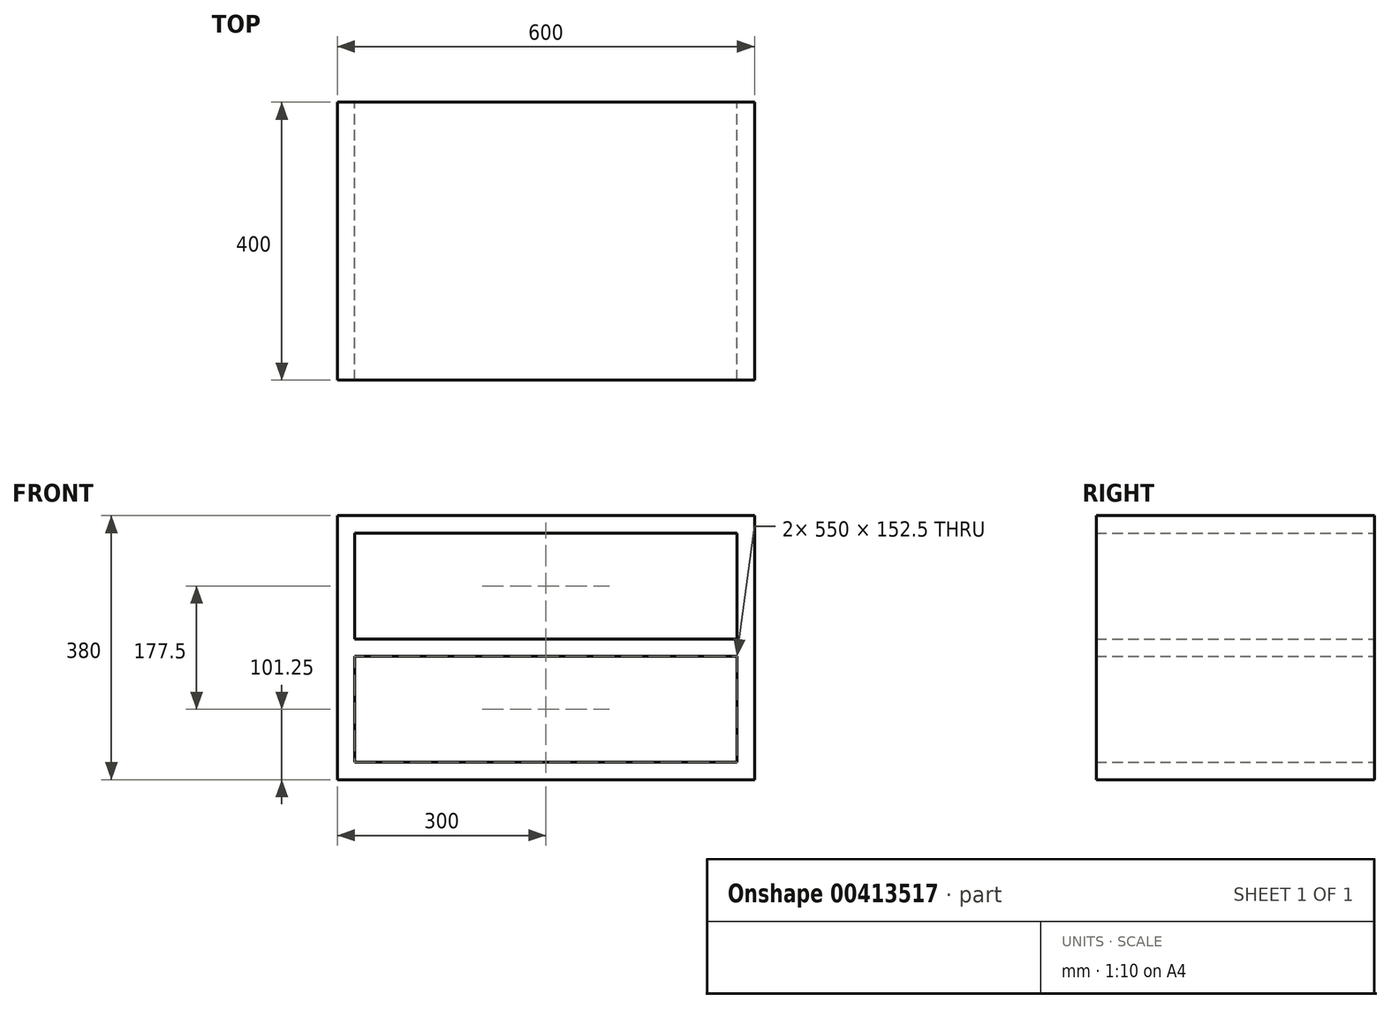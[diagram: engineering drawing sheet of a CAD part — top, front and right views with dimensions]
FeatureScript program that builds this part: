
annotation { "Feature Type Name" : "Feature", "Feature Type Description" : "" }
export const myFeature = defineFeature(function(context is Context, id is Id, definition is map)
    precondition{}
    {
        {
            var Q0;
            Q0=qCreatedBy(makeId("Front.planeOp"),FACE);
            var sketch = newSketch(context, id + "F0", { "sketchPlane" : qUnion([Q0])});
            skLineSegment(sketch, "E0", {"start": v(0, 380) * mm, "end": v(600, 380) * mm});
            skLineSegment(sketch, "E1", {"start": v(600, 380) * mm, "end": v(600, 0) * mm});
            skLineSegment(sketch, "E2", {"start": v(600, 0) * mm, "end": v(0, 0) * mm});
            skLineSegment(sketch, "E3", {"start": v(0, 0) * mm, "end": v(0, 380) * mm});
            skLineSegment(sketch, "E4", {"start": v(25, 355) * mm, "end": v(25, 25) * mm});
            skLineSegment(sketch, "E5", {"start": v(25, 25) * mm, "end": v(575, 25) * mm});
            skLineSegment(sketch, "E6", {"start": v(575, 25) * mm, "end": v(575, 355) * mm});
            skLineSegment(sketch, "E7", {"start": v(575, 355) * mm, "end": v(25, 355) * mm});
            skLineSegment(sketch, "E8", {"start": v(25, 202.5) * mm, "end": v(575, 202.5) * mm});
            skLineSegment(sketch, "E9", {"start": v(25, 177.5) * mm, "end": v(575, 177.5) * mm});
            skSolve(sketch);
        }
        {
            var Q0;
            Q0=makeQuery(id+"F0.imprint","IMPRINT",FACE,{"disambiguationData":[TD([[makeQuery(id+"F0.imprint","IMPRINT",EDGE,{"derivedFrom":sQuery(id+"F0.wireOp",EDGE,"E0")}),-1.0]])]});
            var Q1;
            Q1=makeQuery(id+"F0.imprint","IMPRINT",FACE,{"disambiguationData":[TD([[makeQuery(id+"F0.imprint","IMPRINT",EDGE,{"derivedFrom":sQuery(id+"F0.wireOp",EDGE,"E4")}),1.0]])]});
            extrude(context, id + "F1", {"entities" : qUnion([Q0, Q1]), "offsetDistance" : 25 * mm, "depth" : 50 * mm});
        }
        {
            var Q0;
            Q0=makeQuery(id+"F0.imprint","IMPRINT",FACE,{"disambiguationData":[TD([[makeQuery(id+"F0.imprint","IMPRINT",EDGE,{"derivedFrom":sQuery(id+"F0.wireOp",EDGE,"E0")}),-1.0]])]});
            extrude(context, id + "F2", {"entities" : qUnion([Q0]), "operationType" : NewBodyOperationType.ADD, "offsetDistance" : 25 * mm, "depth" : 400 * mm});
        }
        {
            var Q0;
            Q0=makeQuery(id+"F1.opExtrude","CAP_FACE",FACE,{"disambiguationData":[OSD([sQuery(id+"F0.wireOp",EDGE,"E0"),sQuery(id+"F0.wireOp",EDGE,"E1"),sQuery(id+"F0.wireOp",EDGE,"E2"),sQuery(id+"F0.wireOp",EDGE,"E3")])],"isStart":false});
            extrude(context, id + "F3", {"entities" : qUnion([Q0]), "operationType" : NewBodyOperationType.REMOVE, "endBound" : BoundingType.THROUGH_ALL, "oppositeDirection" : true, "offsetDistance" : 25 * mm, "depth" : 25 * mm});
        }
        {
            var Q0;
            {var subQ2=sQuery(id+"F0.wireOp",EDGE,"E8");Q0=makeQuery(id+"F0.imprint","IMPRINT",FACE,{"disambiguationData":[TD([[makeQuery(id+"F0.imprint","IMPRINT",EDGE,{"derivedFrom":subQ2}),-1.0]])]});}
            var Q1;
            Q1=makeQuery(id+"F2.opExtrude","CAP_FACE",FACE,{"disambiguationData":[OSD([sQuery(id+"F0.wireOp",EDGE,"E0"),sQuery(id+"F0.wireOp",EDGE,"E1"),sQuery(id+"F0.wireOp",EDGE,"E2"),sQuery(id+"F0.wireOp",EDGE,"E3"),sQuery(id+"F0.wireOp",EDGE,"E4"),sQuery(id+"F0.wireOp",EDGE,"E5"),sQuery(id+"F0.wireOp",EDGE,"E6"),sQuery(id+"F0.wireOp",EDGE,"E7")])],"isStart":false});
            extrude(context, id + "F4", {"entities" : qUnion([Q0]), "operationType" : NewBodyOperationType.ADD, "endBound" : BoundingType.UP_TO_SURFACE, "depth" : 25 * mm, "endBoundEntityFace" : qUnion([Q1]), "offsetDistance" : 25 * mm});
        }
    });
